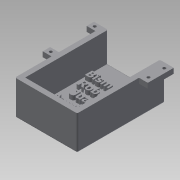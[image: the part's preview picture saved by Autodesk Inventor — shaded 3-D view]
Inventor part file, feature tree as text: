
AUTODESK INVENTOR PART (.ipt)
format: ipt  version: 2015 SP1 (Build 190203100, 203)  size: 1,042,944 bytes
history: native  units: mm
features: sketch x13, extrude x12, projected_geometry x9, fillet x2, reference x2
ambient origin geometry x8: Origin, YZ Plane, XZ Plane, XY Plane, X Axis, Y Axis, Z Axis, Center Point
bodies: Solid1 (feature_tree)
feature tree (38):
  extrude  "Extrusion1"  Depth=60.0mm
  extrude  "Extrusion3"  Depth=3.5mm TaperAngle=0.0deg
  extrude  "Extrusion4"  Depth=3.5mm TaperAngle=0.0deg
  extrude  "Extrusion5"  Depth=3.5mm TaperAngle=0.0deg
  extrude  "Extrusion6"  Depth=6.0mm
  extrude  "Extrusion7"  Depth=3.5mm
  extrude  "Extrusion8"  Depth=2.0mm
  fillet  "Fillet1"  Radius=2.0mm
  extrude  "Extrusion9"  Depth=3.5mm TaperAngle=0.0deg
  extrude  "Extrusion10"  Depth=3.5mm TaperAngle=0.0deg
  fillet  "Fillet2"  Radius=3.5mm
  extrude  "Extrusion11"  Depth=3.5mm TaperAngle=0.0deg
  extrude  "Extrusion12"  TaperAngle=45.0deg  [1 undecoded]
  sketch  "Sketch17"  dims[d63=3.0mm d64=0.0mm]
  extrude  "Extrusion14"  [1 undecoded]
  sketch  "Sketch1"  dims[d0=42.5mm d1=60.0mm]
  sketch  "Sketch4"  dims[d2=3.5mm d3=0.0mm d11=20.0mm d12=0.0mm]
  sketch  "Sketch5"  dims[d13=3.5mm d14=0.0mm d15=3.5mm d16=0.0mm]
  sketch  "Sketch6"  dims[d17=3.5mm d18=0.0mm d19=3.5mm d20=0.0mm]
  sketch  "Sketch7"  dims[d21=6.0mm d22=6.0mm]
  reference  "Reference1"
  sketch  "Sketch8"  dims[d23=3.5mm d24=2.0mm]
  reference  "Reference2"
  sketch  "Sketch11"  dims[d25=2.0mm d26=2.0mm d27=2.0mm]
  projected_geometry  "Projected Loop1"
  projected_geometry  "Projected Loop2"
  projected_geometry  "Projected Loop3"
  sketch  "Sketch12"  dims[d28=3.5mm d29=3.5mm d30=0.0mm]
  sketch  "Sketch13"  dims[d31=1.0mm d32=3.5mm d33=0.0mm d34=3.5mm d35=0.0mm]
  projected_geometry  "Projected Loop4"
  projected_geometry  "Projected Loop5"
  projected_geometry  "Projected Loop6"
  projected_geometry  "Projected Loop7"
  projected_geometry  "Projected Loop8"
  sketch  "Sketch15"  dims[d36=1.0mm d51=3.5mm d52=0.0mm]
  projected_geometry  "Projected Loop9"
  sketch  "Sketch16"  dims[d53=3.5mm d54=0.0mm d57=45.0deg d58=45.0deg d59=135.0deg d60=135.0deg]
  sketch  "Sketch19"
note: 2 required parameter values undecoded (feature->parameter linkage not recoverable at this tier; creation-order binding heuristic only, values carry confidence <= 0.55)
